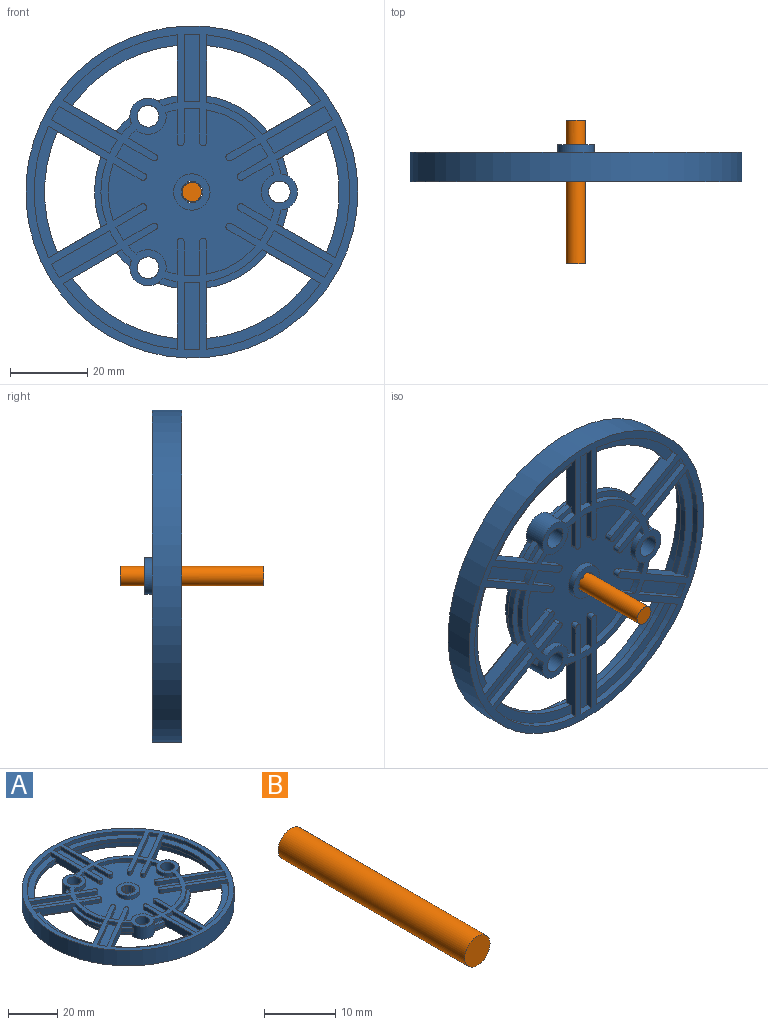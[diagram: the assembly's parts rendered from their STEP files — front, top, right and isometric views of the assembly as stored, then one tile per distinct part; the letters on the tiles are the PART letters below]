
ASSEMBLY  parts=2 mates=1
PART A: 214 faces, bbox 85.9x85.9x9.6 mm
  f0: cylinder r=2.82mm len=9.55mm, axis (0,0,1), area 20.9mm2, adj f103,f111,f210,f211
  f1: cylinder r=2.82mm len=9.55mm, axis (0,0,1), area 20.9mm2, adj f103,f111,f209,f210
  f2: cylinder r=2.82mm len=9.55mm, axis (0,0,1), area 20.9mm2, adj f103,f111,f208,f209
  f3: cylinder r=2.82mm len=9.55mm, axis (0,0,1), area 20.9mm2, adj f103,f111,f207,f208
  f4: cylinder r=2.82mm len=9.55mm, axis (0,0,1), area 20.9mm2, adj f103,f111,f206,f207
  f5: cylinder r=2.82mm len=9.55mm, axis (0,0,1), area 20.9mm2, adj f103,f111,f206,f211
  f6: cylinder r=23.51mm len=6.27mm, axis (0,0,1), area 16.3mm2, adj f35,f105,f130,f204
  f7: plane 4.96x2.8mm, normal (0,0,1), area 7.2mm2, adj f8,f52,f157,f204
  f8: cylinder r=25.15mm len=4.96mm, axis (0,0,1), area 9mm2, adj f7,f35,f157,f204
  f9: cylinder r=23.51mm len=3.62mm, axis (0,0,1), area 6.6mm2, adj f41,f108,f133,f204
  f10: cylinder r=21.6mm len=2.88mm, axis (0,0,1), area 5.2mm2, adj f71,f108,f177,f202
  f11: cylinder r=21.6mm len=5.55mm, axis (0,0,1), area 14.4mm2, adj f25,f105,f195,f203
  f12: cylinder r=21.6mm len=4.49mm, axis (0,0,1), area 14.4mm2, adj f27,f105,f193,f201
  f13: cylinder r=21.6mm len=2.15mm, axis (0,0,1), area 5.2mm2, adj f71,f108,f188,f200
  f14: cylinder r=23.51mm len=6.55mm, axis (0,0,1), area 16.3mm2, adj f37,f105,f128,f199
  f15: plane 4.98x2.57mm, normal (0,0,1), area 7.2mm2, adj f17,f50,f119,f199
  f16: cylinder r=25.15mm len=3.66mm, axis (0,0,1), area 9mm2, adj f37,f45,f150,f199
  f17: cylinder r=23.51mm len=3.65mm, axis (0,0,1), area 6.6mm2, adj f15,f108,f119,f199
  f18: cylinder r=21.6mm len=5.8mm, axis (0,0,1), area 14.4mm2, adj f29,f105,f191,f198
  f19: cylinder r=21.6mm len=2.9mm, axis (0,0,1), area 5.2mm2, adj f71,f108,f183,f197
  f20: cylinder r=23.51mm len=5.07mm, axis (0,0,1), area 16.3mm2, adj f39,f105,f142,f196
  f21: plane 4.49x4.05mm, normal (0,0,1), area 7.2mm2, adj f23,f48,f145,f196
  f22: cylinder r=25.15mm len=4.98mm, axis (0,0,1), area 9mm2, adj f39,f43,f138,f196
  f23: cylinder r=23.51mm len=2.71mm, axis (0,0,1), area 6.6mm2, adj f21,f108,f145,f196
  f24: cylinder r=4.7mm len=9.4mm, axis (0,0,1), area 164.8mm2, adj f25,f27,f29,f103,f105,f190,f191,f192
  f25: plane 31.57x20.21mm, normal (0,0,-1), area 410.7mm2, adj f11,f24,f104,f190,f195,f203
  f26: cylinder r=21.6mm len=24.95mm, axis (0,0,1), area 69.6mm2, adj f27,f105,f194,f201
  f27: plane 36.46x18.5mm, normal (0,0,-1), area 410.7mm2, adj f12,f24,f26,f193,f194,f201
  f28: cylinder r=21.6mm len=26.08mm, axis (0,0,1), area 69.6mm2, adj f29,f105,f192,f198
  f29: plane 31.57x20.68mm, normal (0,0,-1), area 410.7mm2, adj f18,f24,f28,f191,f192,f198
  f30: cylinder r=23.51mm len=6.27mm, axis (0,0,1), area 16.3mm2, adj f35,f105,f155,f204
  f31: cylinder r=23.51mm len=18.95mm, axis (0,0,1), area 55.5mm2, adj f40,f105,f131,f136
  f32: cylinder r=23.51mm len=6.55mm, axis (0,0,1), area 16.3mm2, adj f39,f105,f137,f196
  f33: cylinder r=23.51mm len=21.88mm, axis (0,0,1), area 55.5mm2, adj f38,f105,f143,f148
  f34: cylinder r=23.51mm len=5.07mm, axis (0,0,1), area 16.3mm2, adj f37,f105,f149,f199
  f35: plane 39.2x20.01mm, normal (0,0,-1), area 206.5mm2, adj f6,f8,f30,f46,f92,f98,f130,f133
  f36: plane 33.95x28.26mm, normal (0,0,-1), area 221.2mm2, adj f97,f98,f106,f121,f125,f129,f154,f156
  f37: plane 33.95x28.26mm, normal (0,0,-1), area 206.5mm2, adj f14,f16,f34,f50,f96,f98,f119,f128
  f38: plane 39.2x20.01mm, normal (0,0,-1), area 221.2mm2, adj f33,f49,f95,f98,f143,f144,f148,f151
  f39: plane 33.95x28.26mm, normal (0,0,-1), area 206.5mm2, adj f20,f22,f32,f48,f94,f98,f137,f138
  f40: plane 33.95x28.26mm, normal (0,0,-1), area 221.2mm2, adj f31,f47,f93,f98,f131,f132,f136,f139
  f41: plane 4.96x2.8mm, normal (0,0,1), area 7.2mm2, adj f9,f46,f133,f204
  f42: plane 15.79x9.95mm, normal (0,0,1), area 29.2mm2, adj f47,f54,f132,f139
  f43: plane 4.98x2.57mm, normal (0,0,1), area 7.2mm2, adj f22,f56,f138,f196
  f44: plane 18.23x3.15mm, normal (0,0,1), area 29.2mm2, adj f49,f58,f144,f151
  f45: plane 4.49x4.05mm, normal (0,0,1), area 7.2mm2, adj f16,f60,f150,f199
  f46: cylinder r=25.15mm len=4.96mm, axis (0,0,1), area 9mm2, adj f35,f41,f133,f204
  f47: cylinder r=25.15mm len=15.79mm, axis (0,0,1), area 32.7mm2, adj f40,f42,f132,f139
  f48: cylinder r=25.15mm len=3.66mm, axis (0,0,1), area 9mm2, adj f21,f39,f145,f196
  f49: cylinder r=25.15mm len=18.23mm, axis (0,0,1), area 32.7mm2, adj f38,f44,f144,f151
  f50: cylinder r=25.15mm len=4.98mm, axis (0,0,1), area 9mm2, adj f15,f37,f119,f199
  f51: cylinder r=23.51mm len=3.41mm, axis (0,0,1), area 6.9mm2, adj f82,f108,f158,f159
  f52: cylinder r=23.51mm len=3.62mm, axis (0,0,1), area 6.6mm2, adj f7,f108,f157,f204
  f53: cylinder r=23.51mm len=3.41mm, axis (0,0,1), area 6.9mm2, adj f84,f108,f134,f135
  f54: cylinder r=23.51mm len=14.35mm, axis (0,0,1), area 29.7mm2, adj f42,f108,f132,f139
  f55: cylinder r=23.51mm len=3.94mm, axis (0,0,1), area 6.9mm2, adj f86,f108,f140,f141
  f56: cylinder r=23.51mm len=3.65mm, axis (0,0,1), area 6.6mm2, adj f43,f108,f138,f196
  f57: cylinder r=23.51mm len=3.41mm, axis (0,0,1), area 6.9mm2, adj f88,f108,f146,f147
  f58: cylinder r=23.51mm len=16.57mm, axis (0,0,1), area 29.7mm2, adj f44,f108,f144,f151
  f59: cylinder r=23.51mm len=3.41mm, axis (0,0,1), area 6.9mm2, adj f90,f108,f152,f153
  f60: cylinder r=23.51mm len=2.71mm, axis (0,0,1), area 6.6mm2, adj f45,f108,f150,f199
  f61: cylinder r=21.6mm len=3.41mm, axis (0,0,1), area 6.9mm2, adj f71,f108,f174,f176
  f62: cylinder r=21.6mm len=2.88mm, axis (0,0,1), area 5.2mm2, adj f71,f108,f170,f202
  f63: cylinder r=21.6mm len=3.41mm, axis (0,0,1), area 6.9mm2, adj f71,f108,f167,f171
  f64: cylinder r=21.6mm len=12.68mm, axis (0,0,1), area 26.2mm2, adj f71,f108,f168,f179
  f65: cylinder r=21.6mm len=3.94mm, axis (0,0,1), area 6.9mm2, adj f71,f108,f180,f182
  f66: cylinder r=21.6mm len=2.15mm, axis (0,0,1), area 5.2mm2, adj f71,f108,f164,f197
  f67: cylinder r=21.6mm len=3.41mm, axis (0,0,1), area 6.9mm2, adj f71,f108,f161,f165
  f68: cylinder r=21.6mm len=14.64mm, axis (0,0,1), area 26.2mm2, adj f71,f108,f162,f185
  f69: cylinder r=21.6mm len=3.41mm, axis (0,0,1), area 6.9mm2, adj f71,f108,f186,f189
  f70: cylinder r=21.6mm len=2.9mm, axis (0,0,1), area 5.2mm2, adj f71,f108,f116,f200
  f71: plane 43.21x42.74mm, normal (0,0,1), area 1121mm2, adj f10,f13,f19,f61,f62,f63,f64,f65
  f72: cylinder r=40.82mm len=3.41mm, axis (0,0,1), area 6.9mm2, adj f82,f108,f158,f159
  f73: cylinder r=40.82mm len=34.02mm, axis (0,0,1), area 61.5mm2, adj f85,f108,f133,f157
  f74: cylinder r=40.82mm len=3.41mm, axis (0,0,1), area 6.9mm2, adj f84,f108,f134,f135
  f75: cylinder r=40.82mm len=29.46mm, axis (0,0,1), area 61.5mm2, adj f87,f108,f132,f139
  f76: cylinder r=40.82mm len=3.94mm, axis (0,0,1), area 6.9mm2, adj f86,f108,f140,f141
  f77: cylinder r=40.82mm len=29.46mm, axis (0,0,1), area 61.5mm2, adj f89,f108,f138,f145
  f78: cylinder r=40.82mm len=3.41mm, axis (0,0,1), area 6.9mm2, adj f88,f108,f146,f147
  f79: cylinder r=40.82mm len=34.02mm, axis (0,0,1), area 61.5mm2, adj f91,f108,f144,f151
  f80: cylinder r=40.82mm len=3.41mm, axis (0,0,1), area 6.9mm2, adj f90,f108,f152,f153
  f81: cylinder r=40.82mm len=29.46mm, axis (0,0,1), area 61.5mm2, adj f108,f119,f124,f150
  f82: plane 16.99x12.08mm, normal (0,0,1), area 68.2mm2, adj f51,f72,f158,f159
  f83: plane 29.46x18.37mm, normal (0,0,1), area 91.5mm2, adj f121,f123,f125,f156
  f84: plane 16.99x12.08mm, normal (0,0,1), area 68.2mm2, adj f53,f74,f134,f135
  f85: plane 34.02x6.08mm, normal (0,0,1), area 91.5mm2, adj f73,f92,f133,f157
  f86: plane 17.39x3.94mm, normal (0,0,1), area 68.2mm2, adj f55,f76,f140,f141
  f87: plane 29.46x18.37mm, normal (0,0,1), area 91.5mm2, adj f75,f93,f132,f139
  f88: plane 16.99x12.08mm, normal (0,0,1), area 68.2mm2, adj f57,f78,f146,f147
  f89: plane 29.46x18.37mm, normal (0,0,1), area 91.5mm2, adj f77,f94,f138,f145
  f90: plane 16.99x12.08mm, normal (0,0,1), area 68.2mm2, adj f59,f80,f152,f153
  f91: plane 34.02x6.08mm, normal (0,0,1), area 91.5mm2, adj f79,f95,f144,f151
  f92: cylinder r=38.1mm len=31.29mm, axis (0,0,1), area 56.5mm2, adj f35,f85,f133,f157
  f93: cylinder r=38.1mm len=27.1mm, axis (0,0,1), area 56.5mm2, adj f40,f87,f132,f139
  f94: cylinder r=38.1mm len=27.1mm, axis (0,0,1), area 56.5mm2, adj f39,f89,f138,f145
  f95: cylinder r=38.1mm len=31.29mm, axis (0,0,1), area 56.5mm2, adj f38,f91,f144,f151
  f96: cylinder r=38.1mm len=27.1mm, axis (0,0,1), area 56.5mm2, adj f37,f119,f124,f150
  f97: cylinder r=23.51mm len=18.95mm, axis (0,0,1), area 55.5mm2, adj f36,f105,f129,f154
  f98: cylinder r=40.82mm len=81.64mm, axis (0,0,1), area 1021.7mm2, adj f35,f36,f37,f38,f39,f40,f105,f126
  f99: plane 15.79x9.95mm, normal (0,0,1), area 29.2mm2, adj f106,f107,f121,f156
  f100: plane 17.39x3.94mm, normal (0,0,1), area 68.2mm2, adj f101,f118,f120,f122
  f101: cylinder r=23.51mm len=3.94mm, axis (0,0,1), area 6.9mm2, adj f100,f108,f118,f120
  f102: cylinder r=21.6mm len=3.94mm, axis (0,0,1), area 6.9mm2, adj f71,f108,f114,f117
  f103: plane 9.4x9.4mm, normal (0,0,-1), area 45.8mm2, adj f0,f1,f2,f3,f4,f5,f24,f206
  f104: cylinder r=21.6mm len=20.21mm, axis (0,0,1), area 69.6mm2, adj f25,f105,f190,f203
  f105: plane 81.64x71.61mm, normal (0,0,-1), area 635.6mm2, adj f6,f11,f12,f14,f18,f20,f24,f26
  f106: cylinder r=25.15mm len=15.79mm, axis (0,0,1), area 32.7mm2, adj f36,f99,f121,f156
  f107: cylinder r=23.51mm len=14.35mm, axis (0,0,1), area 29.7mm2, adj f99,f108,f121,f156
  f108: plane 85.88x85.88mm, normal (0,0,1), area 1499mm2, adj f9,f10,f13,f17,f19,f23,f51,f52
  f109: cylinder r=21.6mm len=12.68mm, axis (0,0,1), area 26.2mm2, adj f71,f108,f113,f173
  f110: cylinder r=4.7mm len=9.4mm, axis (0,0,1), area 51.7mm2, adj f71,f111
  f111: plane 9.4x9.4mm, normal (0,0,1), area 45.8mm2, adj f0,f1,f2,f3,f4,f5,f110,f206
  f112: cylinder r=0.93mm len=1.85mm, axis (0,0,1), area 5.1mm2, adj f71,f108,f113,f114
  f113: plane 8.35x1.75mm, normal (1,0,0), area 14.6mm2, adj f71,f108,f109,f112
  f114: plane 8.61x1.75mm, normal (-1,0,0), area 15.1mm2, adj f71,f102,f108,f112
  f115: cylinder r=0.93mm len=1.85mm, axis (0,0,1), area 5.1mm2, adj f71,f108,f116,f117
  f116: plane 8.35x1.75mm, normal (-1,0,0), area 14.6mm2, adj f70,f71,f108,f115
  f117: plane 8.61x1.75mm, normal (1,0,0), area 15.1mm2, adj f71,f102,f108,f115
  f118: plane 17.35x1.75mm, normal (1,0,0), area 30.4mm2, adj f100,f101,f108,f122
  f119: plane 17.44x3.51mm, normal (-1,0,0), area 53.5mm2, adj f15,f17,f37,f50,f81,f96,f108,f124
  f120: plane 17.35x1.75mm, normal (-1,0,0), area 30.4mm2, adj f100,f101,f108,f122
  f121: plane 17.44x3.51mm, normal (1,0,0), area 53.5mm2, adj f36,f83,f99,f106,f107,f108,f123,f125
  f122: cylinder r=40.82mm len=3.94mm, axis (0,0,1), area 6.9mm2, adj f100,f108,f118,f120
  f123: cylinder r=40.82mm len=29.46mm, axis (0,0,1), area 61.5mm2, adj f83,f108,f121,f156
  f124: plane 29.46x18.37mm, normal (0,0,1), area 91.5mm2, adj f81,f96,f119,f150
  f125: cylinder r=38.1mm len=27.1mm, axis (0,0,1), area 56.5mm2, adj f36,f83,f121,f156
  f126: plane 85.88x85.88mm, normal (0,0,-1), area 558.1mm2, adj f98,f127
  f127: cylinder r=42.94mm len=85.88mm, axis (0,0,1), area 2049mm2, adj f108,f126
  f128: plane 17.32x2.44mm, normal (-1,0,0), area 42.2mm2, adj f14,f37,f98,f105
  f129: plane 17.32x2.44mm, normal (1,0,0), area 42.2mm2, adj f36,f97,f98,f105
  f130: plane 15x8.66mm, normal (0.5,0.87,0), area 42.2mm2, adj f6,f35,f98,f105
  f131: plane 15x8.66mm, normal (-0.5,-0.87,0), area 42.2mm2, adj f31,f40,f98,f105
  f132: plane 15.11x8.72mm, normal (-0.5,-0.87,0), area 53.5mm2, adj f40,f42,f47,f54,f75,f87,f93,f108
  f133: plane 15.11x8.72mm, normal (0.5,0.87,0), area 53.5mm2, adj f9,f35,f41,f46,f73,f85,f92,f108
  f134: plane 15.02x8.67mm, normal (0.5,0.87,0), area 30.4mm2, adj f53,f74,f84,f108
  f135: plane 15.02x8.67mm, normal (-0.5,-0.87,0), area 30.4mm2, adj f53,f74,f84,f108
  f136: plane 17.32x2.44mm, normal (1,0,0), area 42.2mm2, adj f31,f40,f98,f105
  f137: plane 17.32x2.44mm, normal (-1,0,0), area 42.2mm2, adj f32,f39,f98,f105
  f138: plane 17.44x3.51mm, normal (-1,0,0), area 53.5mm2, adj f22,f39,f43,f56,f77,f89,f94,f108
  f139: plane 17.44x3.51mm, normal (1,0,0), area 53.5mm2, adj f40,f42,f47,f54,f75,f87,f93,f108
  f140: plane 17.35x1.75mm, normal (1,0,0), area 30.4mm2, adj f55,f76,f86,f108
  f141: plane 17.35x1.75mm, normal (-1,0,0), area 30.4mm2, adj f55,f76,f86,f108
  f142: plane 15x8.66mm, normal (0.5,-0.87,0), area 42.2mm2, adj f20,f39,f98,f105
  f143: plane 15x8.66mm, normal (-0.5,0.87,0), area 42.2mm2, adj f33,f38,f98,f105
  f144: plane 15.11x8.72mm, normal (-0.5,0.87,0), area 53.5mm2, adj f38,f44,f49,f58,f79,f91,f95,f108
  f145: plane 15.11x8.72mm, normal (0.5,-0.87,0), area 53.5mm2, adj f21,f23,f39,f48,f77,f89,f94,f108
  f146: plane 15.02x8.67mm, normal (0.5,-0.87,0), area 30.4mm2, adj f57,f78,f88,f108
  f147: plane 15.02x8.67mm, normal (-0.5,0.87,0), area 30.4mm2, adj f57,f78,f88,f108
  f148: plane 15x8.66mm, normal (-0.5,-0.87,0), area 42.2mm2, adj f33,f38,f98,f105
  f149: plane 15x8.66mm, normal (0.5,0.87,0), area 42.2mm2, adj f34,f37,f98,f105
  f150: plane 15.11x8.72mm, normal (0.5,0.87,0), area 53.5mm2, adj f16,f37,f45,f60,f81,f96,f108,f124
  f151: plane 15.11x8.72mm, normal (-0.5,-0.87,0), area 53.5mm2, adj f38,f44,f49,f58,f79,f91,f95,f108
  f152: plane 15.02x8.67mm, normal (-0.5,-0.87,0), area 30.4mm2, adj f59,f80,f90,f108
  f153: plane 15.02x8.67mm, normal (0.5,0.87,0), area 30.4mm2, adj f59,f80,f90,f108
  f154: plane 15x8.66mm, normal (-0.5,0.87,0), area 42.2mm2, adj f36,f97,f98,f105
  f155: plane 15x8.66mm, normal (0.5,-0.87,0), area 42.2mm2, adj f30,f35,f98,f105
  f156: plane 15.11x8.72mm, normal (-0.5,0.87,0), area 53.5mm2, adj f36,f83,f99,f106,f107,f108,f123,f125
  f157: plane 15.11x8.72mm, normal (0.5,-0.87,0), area 53.5mm2, adj f7,f8,f35,f52,f73,f85,f92,f108
  f158: plane 15.02x8.67mm, normal (0.5,-0.87,0), area 30.4mm2, adj f51,f72,f82,f108
  f159: plane 15.02x8.67mm, normal (-0.5,0.87,0), area 30.4mm2, adj f51,f72,f82,f108
  f160: cylinder r=0.93mm len=1.75mm, axis (0,0,1), area 5.1mm2, adj f71,f108,f161,f162
  f161: plane 7.45x4.3mm, normal (0.5,-0.87,0), area 15.1mm2, adj f67,f71,f108,f160
  f162: plane 7.23x4.18mm, normal (-0.5,0.87,0), area 14.6mm2, adj f68,f71,f108,f160
  f163: cylinder r=0.93mm len=1.75mm, axis (0,0,1), area 5.1mm2, adj f71,f108,f164,f165
  f164: plane 7.23x4.18mm, normal (0.5,-0.87,0), area 14.6mm2, adj f66,f71,f108,f163
  f165: plane 7.45x4.3mm, normal (-0.5,0.87,0), area 15.1mm2, adj f67,f71,f108,f163
  f166: cylinder r=0.93mm len=1.75mm, axis (0,0,1), area 5.1mm2, adj f71,f108,f167,f168
  f167: plane 7.45x4.3mm, normal (0.5,0.87,0), area 15.1mm2, adj f63,f71,f108,f166
  f168: plane 7.23x4.18mm, normal (-0.5,-0.87,0), area 14.6mm2, adj f64,f71,f108,f166
  f169: cylinder r=0.93mm len=1.75mm, axis (0,0,1), area 5.1mm2, adj f71,f108,f170,f171
  f170: plane 7.23x4.18mm, normal (0.5,0.87,0), area 14.6mm2, adj f62,f71,f108,f169
  f171: plane 7.45x4.3mm, normal (-0.5,-0.87,0), area 15.1mm2, adj f63,f71,f108,f169
  f172: cylinder r=0.93mm len=1.75mm, axis (0,0,1), area 5.1mm2, adj f71,f108,f173,f174
  f173: plane 7.23x4.18mm, normal (-0.5,0.87,0), area 14.6mm2, adj f71,f108,f109,f172
  f174: plane 7.45x4.3mm, normal (0.5,-0.87,0), area 15.1mm2, adj f61,f71,f108,f172
  f175: cylinder r=0.93mm len=1.75mm, axis (0,0,1), area 5.1mm2, adj f71,f108,f176,f177
  f176: plane 7.45x4.3mm, normal (-0.5,0.87,0), area 15.1mm2, adj f61,f71,f108,f175
  f177: plane 7.23x4.18mm, normal (0.5,-0.87,0), area 14.6mm2, adj f10,f71,f108,f175
  f178: cylinder r=0.93mm len=1.85mm, axis (0,0,1), area 5.1mm2, adj f71,f108,f179,f180
  f179: plane 8.35x1.75mm, normal (1,0,0), area 14.6mm2, adj f64,f71,f108,f178
  f180: plane 8.61x1.75mm, normal (-1,0,0), area 15.1mm2, adj f65,f71,f108,f178
  f181: cylinder r=0.93mm len=1.85mm, axis (0,0,1), area 5.1mm2, adj f71,f108,f182,f183
  f182: plane 8.61x1.75mm, normal (1,0,0), area 15.1mm2, adj f65,f71,f108,f181
  f183: plane 8.35x1.75mm, normal (-1,0,0), area 14.6mm2, adj f19,f71,f108,f181
  f184: cylinder r=0.93mm len=1.75mm, axis (0,0,1), area 5.1mm2, adj f71,f108,f185,f186
  f185: plane 7.23x4.18mm, normal (-0.5,-0.87,0), area 14.6mm2, adj f68,f71,f108,f184
  f186: plane 7.45x4.3mm, normal (0.5,0.87,0), area 15.1mm2, adj f69,f71,f108,f184
  f187: cylinder r=0.93mm len=1.75mm, axis (0,0,1), area 5.1mm2, adj f71,f108,f188,f189
  f188: plane 7.23x4.18mm, normal (0.5,0.87,0), area 14.6mm2, adj f13,f71,f108,f187
  f189: plane 7.45x4.3mm, normal (-0.5,-0.87,0), area 15.1mm2, adj f69,f71,f108,f187
  f190: plane 16.98x2.44mm, normal (1,0,0), area 41.4mm2, adj f24,f25,f104,f105
  f191: plane 16.98x2.44mm, normal (-1,0,0), area 41.4mm2, adj f18,f24,f29,f105
  f192: plane 14.7x8.49mm, normal (-0.5,-0.87,0), area 41.4mm2, adj f24,f28,f29,f105
  f193: plane 14.7x8.49mm, normal (0.5,0.87,0), area 41.4mm2, adj f12,f24,f27,f105
  f194: plane 14.7x8.49mm, normal (-0.5,0.87,0), area 41.4mm2, adj f24,f26,f27,f105
  f195: plane 14.7x8.49mm, normal (0.5,-0.87,0), area 41.4mm2, adj f11,f24,f25,f105
  f196: cylinder r=4.69mm len=8.52mm, axis (0,0,1), area 76.1mm2, adj f20,f21,f22,f23,f32,f39,f43,f48
  f197: cylinder r=4.69mm len=7.79mm, axis (0,0,1), area 20.5mm2, adj f19,f66,f71,f108
  f198: cylinder r=4.69mm len=7.79mm, axis (0,0,1), area 28.5mm2, adj f18,f28,f29,f105
  f199: cylinder r=4.69mm len=8.52mm, axis (0,0,1), area 76.1mm2, adj f14,f15,f16,f17,f34,f37,f45,f50
  f200: cylinder r=4.69mm len=7.79mm, axis (0,0,1), area 20.5mm2, adj f13,f70,f71,f108
  f201: cylinder r=4.69mm len=7.79mm, axis (0,0,1), area 28.5mm2, adj f12,f26,f27,f105
  f202: cylinder r=4.69mm len=8.89mm, axis (0,0,1), area 20.5mm2, adj f10,f62,f71,f108
  f203: cylinder r=4.69mm len=8.89mm, axis (0,0,1), area 28.5mm2, adj f11,f25,f104,f105
  f204: cylinder r=4.69mm len=9.34mm, axis (0,0,1), area 76.1mm2, adj f6,f7,f8,f9,f30,f35,f41,f46
  f205: cylinder r=2.82mm len=5.94mm, axis (0,0,1), area 105.3mm2, adj f105,f108
  f206: cylinder r=0.38mm len=9.55mm, axis (0,0,1), area 11.4mm2, adj f4,f5,f103,f111
  f207: cylinder r=0.38mm len=9.55mm, axis (0,0,1), area 11.4mm2, adj f3,f4,f103,f111
  f208: cylinder r=0.38mm len=9.55mm, axis (0,0,1), area 11.4mm2, adj f2,f3,f103,f111
  f209: cylinder r=0.38mm len=9.55mm, axis (0,0,1), area 11.4mm2, adj f1,f2,f103,f111
  f210: cylinder r=0.38mm len=9.55mm, axis (0,0,1), area 11.4mm2, adj f0,f1,f103,f111
  f211: cylinder r=0.38mm len=9.55mm, axis (0,0,1), area 11.4mm2, adj f0,f5,f103,f111
  f212: cylinder r=2.82mm len=5.94mm, axis (0,0,1), area 105.3mm2, adj f105,f108
  f213: cylinder r=2.82mm len=5.94mm, axis (0,0,1), area 105.3mm2, adj f105,f108
PART B: 3 faces, bbox 5x37x5 mm
  f0: plane 5x5mm, normal (0,1,0), area 19.6mm2, adj f1
  f1: cylinder r=2.5mm len=37mm, axis (0,-1,0), area 581.2mm2, adj f0,f2
  f2: plane 5x5mm, normal (0,-1,0), area 19.6mm2, adj f1
PLACE A rot(axis=(1,0,0),90deg) t=(-21.51,-9.55,-0.53)mm
PLACE B t=(-21.51,6.28,-0.53)mm
MATE cylindrical A.f0 <-> B.f1  axis (0,-1,0) through (-21.51,-7.8,-0.53)mm
